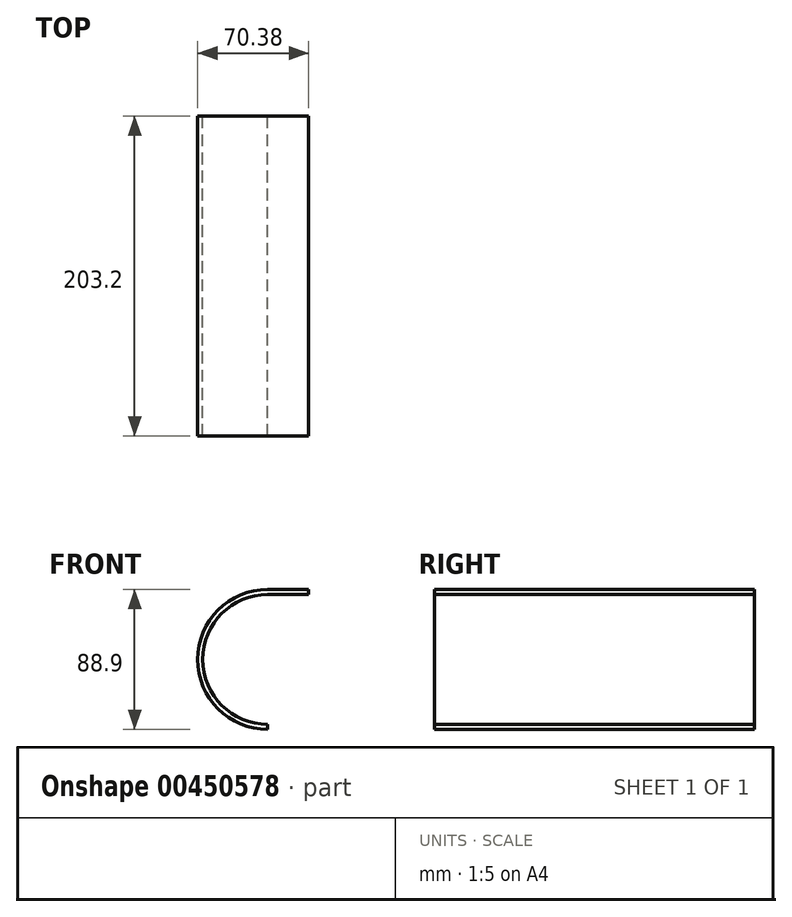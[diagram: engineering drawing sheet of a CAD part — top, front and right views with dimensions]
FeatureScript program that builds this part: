
annotation { "Feature Type Name" : "Feature", "Feature Type Description" : "" }
export const myFeature = defineFeature(function(context is Context, id is Id, definition is map)
    precondition{}
    {
        {
            var Q0;
            Q0=qCreatedBy(makeId("Front.planeOp"),FACE);
            var sketch = newSketch(context, id + "F0", { "sketchPlane" : qUnion([Q0])});
            skArc(sketch, "E0", {"start": v(0, 41.28) * mm, "mid": v(-41.28, 0) * mm, "end": v(0, -41.28) * mm});
            skLineSegment(sketch, "E1", {"start": v(0, 41.28) * mm, "end": v(0, -41.28) * mm, "construction": true});
            skPoint(sketch, "E2.orphan", {"position": v(0, 128) * mm});
            skArc(sketch, "E3.0", {"start": v(0, 44.45) * mm, "mid": v(-44.45, 0) * mm, "end": v(0, -44.45) * mm});
            skLineSegment(sketch, "E4", {"start": v(0, -41.28) * mm, "end": v(0, -44.45) * mm});
            skLineSegment(sketch, "E5", {"start": v(0, 44.45) * mm, "end": v(25.93, 44.45) * mm});
            skLineSegment(sketch, "E6", {"start": v(25.93, 44.45) * mm, "end": v(25.93, 41.28) * mm});
            skLineSegment(sketch, "E7", {"start": v(25.93, 41.28) * mm, "end": v(0, 41.28) * mm});
            skSolve(sketch);
        }
        {
            var Q0;
            Q0=makeQuery(id+"F0.imprint","IMPRINT",FACE,{"disambiguationData":[TD([[makeQuery(id+"F0.imprint","IMPRINT",EDGE,{"derivedFrom":sQuery(id+"F0.wireOp",EDGE,"E0")}),-1.0]])]});
            extrude(context, id + "F1", {"entities" : qUnion([Q0]), "depth" : 203.2 * mm});
        }
    });
